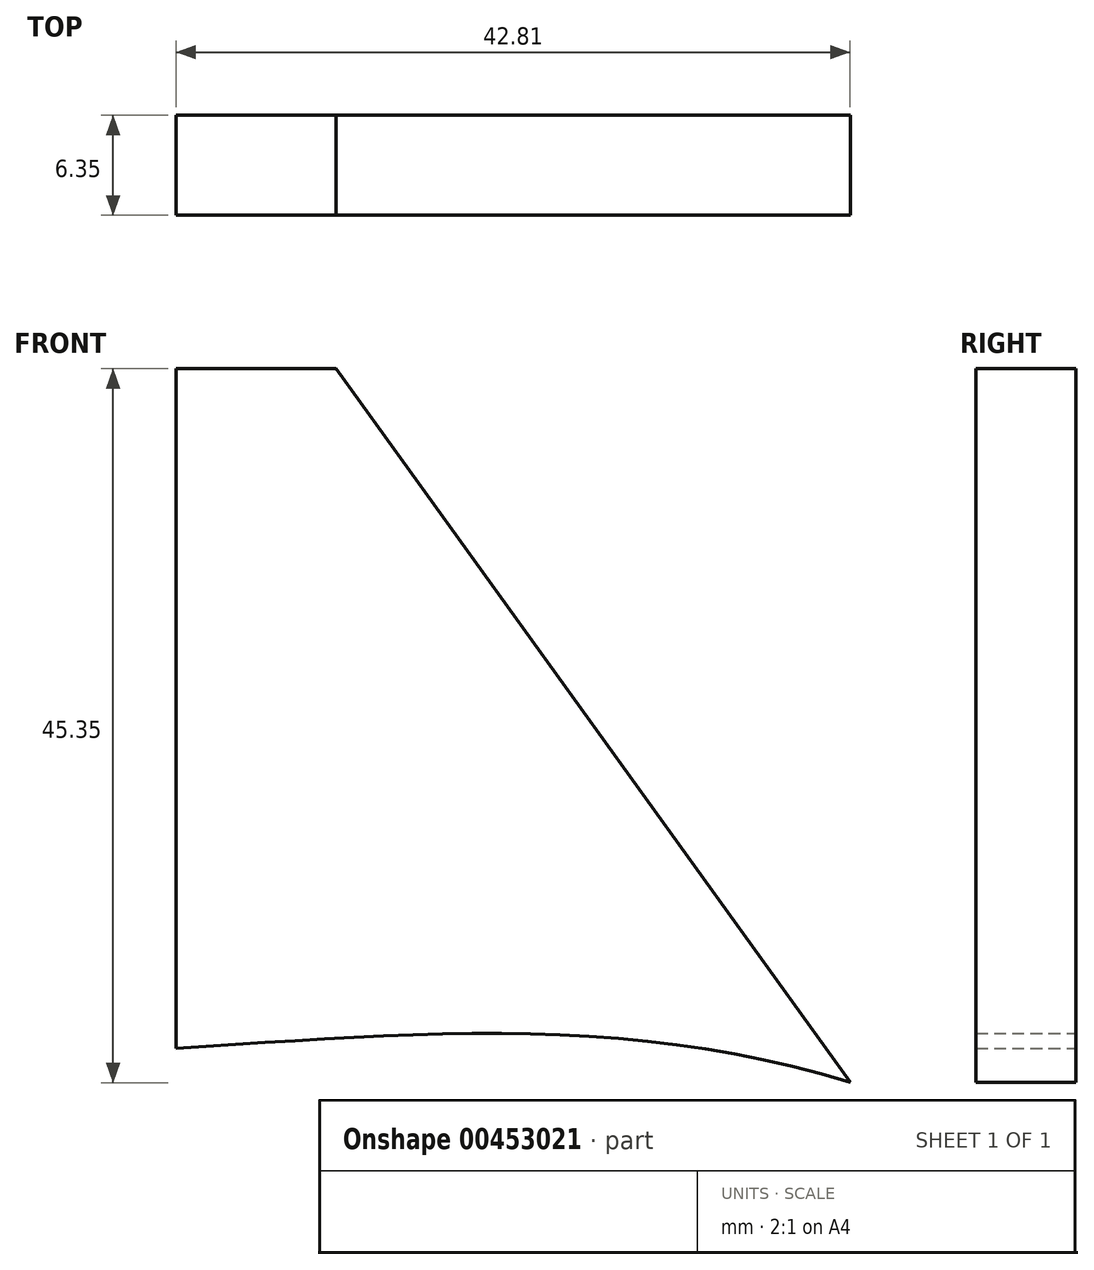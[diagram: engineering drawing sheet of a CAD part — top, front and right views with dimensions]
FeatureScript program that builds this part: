
annotation { "Feature Type Name" : "Feature", "Feature Type Description" : "" }
export const myFeature = defineFeature(function(context is Context, id is Id, definition is map)
    precondition{}
    {
        {
            var Q0;
            Q0=qCreatedBy(makeId("Front.planeOp"),FACE);
            var sketch = newSketch(context, id + "F0", { "sketchPlane" : qUnion([Q0])});
            skLineSegment(sketch, "E0", {"start": v(-53.88, 48.82) * mm, "end": v(-53.88, 5.64) * mm});
            skLineSegment(sketch, "E1", {"start": v(-53.88, 48.82) * mm, "end": v(-43.72, 48.82) * mm});
            skLineSegment(sketch, "E2", {"start": v(-43.72, 48.82) * mm, "end": v(-11.07, 3.47) * mm});
            skFitSpline(sketch, "E3", {"points": [v(-53.88, 5.64) * mm, v(-11.07, 3.47) * mm, v(35.72, -26.16) * mm], "startDerivative": vector(92.9, 6.13) * mm, "endDerivative": vector(86.45, -68.28) * mm});
            skSolve(sketch);
        }
        {
            var Q0;
            Q0 = qSketchRegion(id + "F0", true);
            extrude(context, id + "F1", {"entities" : qUnion([Q0]), "depth" : 6.35 * mm});
        }
    });
